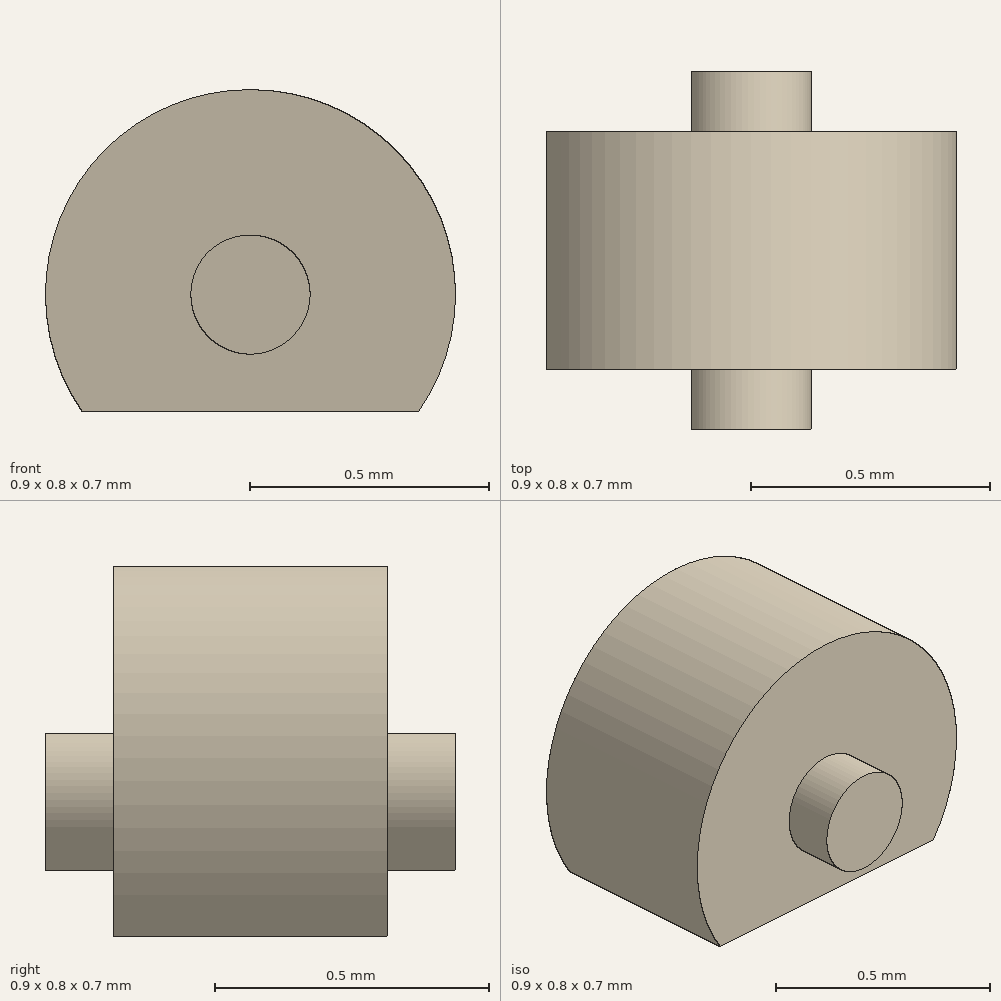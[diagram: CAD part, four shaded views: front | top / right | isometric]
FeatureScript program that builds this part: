
annotation { "Feature Type Name" : "Feature", "Feature Type Description" : "" }
export const myFeature = defineFeature(function(context is Context, id is Id, definition is map)
    precondition{}
    {
        {
            var Q0;
            Q0=qCreatedBy(makeId("Front.planeOp"),FACE);
            var sketch = newSketch(context, id + "F0", { "sketchPlane" : qUnion([Q0])});
            skCircle(sketch, "E0", {"center": v(0, 0) * mm, "radius": 0.43 * mm});
            skCircle(sketch, "E1", {"center": v(0, 0) * mm, "radius": 0.12 * mm});
            skLineSegment(sketch, "E2.bottom", {"start": v(-0.6, -0.24) * mm, "end": v(0.68, -0.24) * mm});
            skLineSegment(sketch, "E2.top", {"start": v(-0.6, -0.78) * mm, "end": v(0.68, -0.78) * mm});
            skLineSegment(sketch, "E2.left", {"start": v(-0.6, -0.24) * mm, "end": v(-0.6, -0.78) * mm});
            skLineSegment(sketch, "E2.right", {"start": v(0.68, -0.24) * mm, "end": v(0.68, -0.78) * mm});
            skSolve(sketch);
        }
        {
            var Q0;
            Q0=makeQuery(id+"F0.imprint","IMPRINT",FACE,{"disambiguationData":[TD([[makeQuery(id+"F0.imprint","IMPRINT",EDGE,{"derivedFrom":sQuery(id+"F0.wireOp",EDGE,"E1")}),-1.0]])]});
            extrude(context, id + "F1", {"entities" : qUnion([Q0]), "depth" : 0.5 * mm, "offsetDistance" : 25 * mm});
        }
        {
            var Q0;
            Q0=makeQuery(id+"F0.imprint","IMPRINT",FACE,{"disambiguationData":[TD([[makeQuery(id+"F0.imprint","IMPRINT",EDGE,{"derivedFrom":sQuery(id+"F0.wireOp",EDGE,"E1")}),1.0]])]});
            extrude(context, id + "F2", {"entities" : qUnion([Q0]), "operationType" : NewBodyOperationType.ADD, "depth" : 0.62 * mm, "offsetDistance" : 25 * mm, "hasSecondDirection" : true, "secondDirectionOppositeDirection" : true, "secondDirectionDepth" : 0.12 * mm});
        }
        {
            var Q0;
            Q0=makeQuery(id+"F1.opExtrude","SWEPT_FACE",FACE,{"disambiguationData":[OSD([sQuery(id+"F0.wireOp",EDGE,"E2.bottom")])]});
            var sketch = newSketch(context, id + "F3", { "sketchPlane" : qUnion([Q0])});
            skCircle(sketch, "E3", {"center": v(0, 0.25) * mm, "radius": 0.12 * mm});
            skSolve(sketch);
        }
        {
            var Q0;
            Q0=makeQuery(id+"F3.imprint","IMPRINT",FACE,{"disambiguationData":[TD([[makeQuery(id+"F3.imprint","IMPRINT",EDGE,{"derivedFrom":sQuery(id+"F3.wireOp",EDGE,"E3")}),1.0]])]});
            extrude(context, id + "F4", {"entities" : qUnion([Q0]), "operationType" : NewBodyOperationType.REMOVE, "oppositeDirection" : true, "depth" : 0.5 * mm, "offsetDistance" : 25 * mm});
        }
    });
